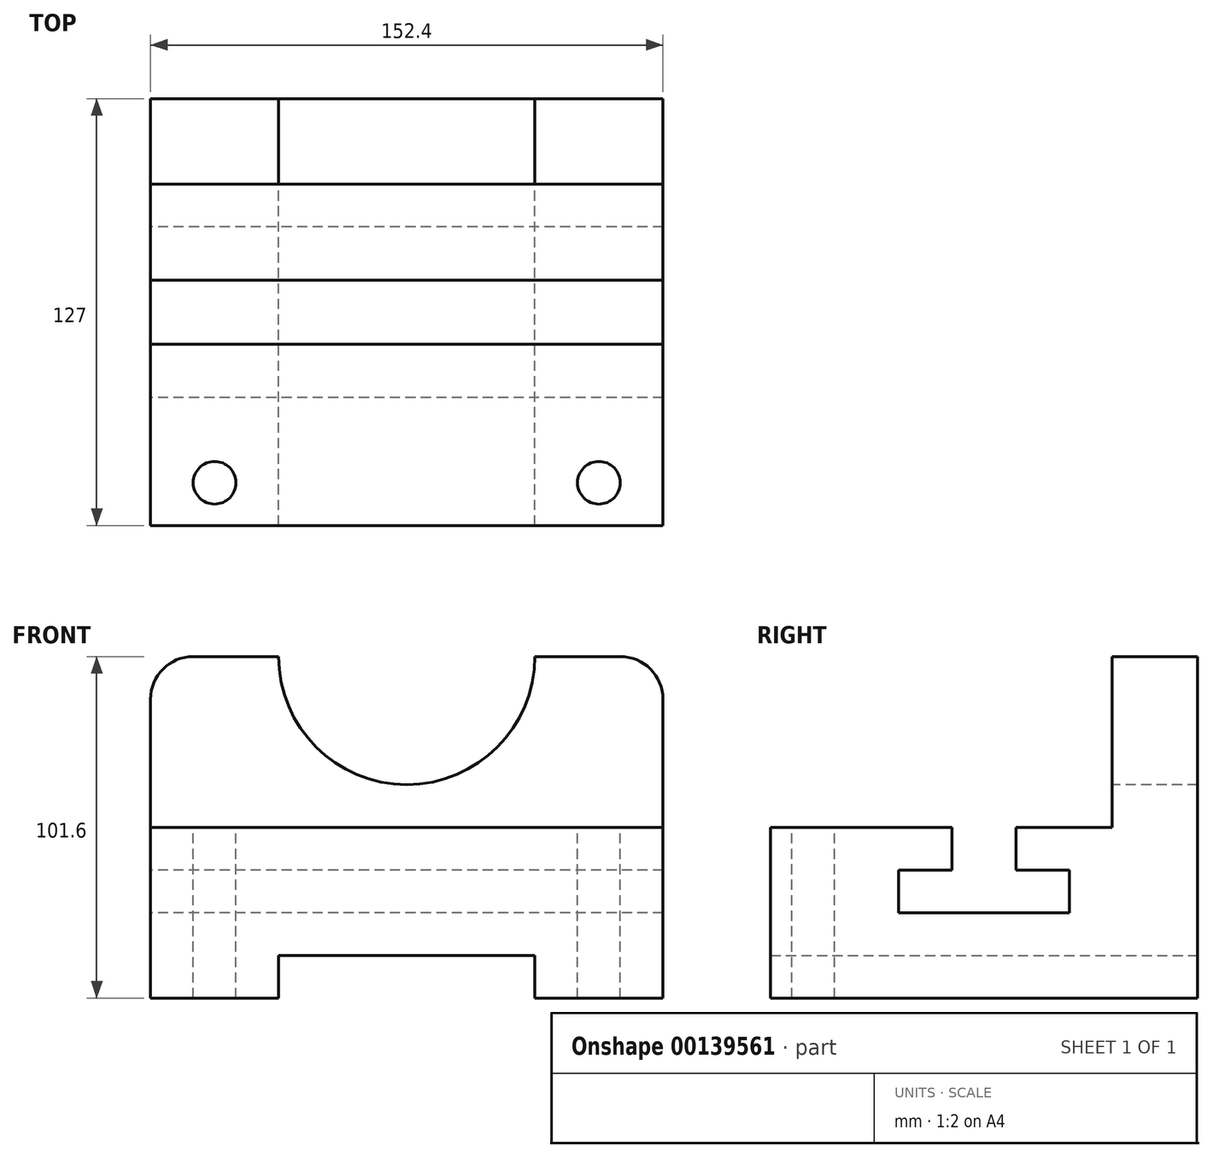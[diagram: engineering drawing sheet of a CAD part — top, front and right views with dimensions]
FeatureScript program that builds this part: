
annotation { "Feature Type Name" : "Feature", "Feature Type Description" : "" }
export const myFeature = defineFeature(function(context is Context, id is Id, definition is map)
    precondition{}
    {
        {
            var Q0;
            Q0=qCreatedBy(makeId("Right.planeOp"),FACE);
            var sketch = newSketch(context, id + "F0", { "sketchPlane" : qUnion([Q0])});
            skLineSegment(sketch, "E0", {"start": v(0, 0) * mm, "end": v(-127, 0) * mm});
            skLineSegment(sketch, "E1", {"start": v(0, 0) * mm, "end": v(0, 50.8) * mm});
            skLineSegment(sketch, "E2", {"start": v(0, 50.8) * mm, "end": v(-127, 50.8) * mm});
            skLineSegment(sketch, "E3", {"start": v(-127, 50.8) * mm, "end": v(-127, 0) * mm});
            skLineSegment(sketch, "E4", {"start": v(-53.98, 50.8) * mm, "end": v(-53.98, 38.1) * mm});
            skLineSegment(sketch, "E5", {"start": v(0, 50.8) * mm, "end": v(0, 101.6) * mm});
            skLineSegment(sketch, "E6", {"start": v(0, 101.6) * mm, "end": v(-25.4, 101.6) * mm});
            skLineSegment(sketch, "E7", {"start": v(-25.4, 101.6) * mm, "end": v(-25.4, 50.8) * mm});
            skLineSegment(sketch, "E8", {"start": v(-53.98, 38.1) * mm, "end": v(-38.1, 38.1) * mm});
            skLineSegment(sketch, "E9", {"start": v(-38.1, 38.1) * mm, "end": v(-38.1, 25.4) * mm});
            skLineSegment(sketch, "E10", {"start": v(-38.1, 25.4) * mm, "end": v(-88.9, 25.4) * mm});
            skLineSegment(sketch, "E11", {"start": v(-88.9, 25.4) * mm, "end": v(-88.9, 38.1) * mm});
            skLineSegment(sketch, "E12", {"start": v(-88.9, 38.1) * mm, "end": v(-73.03, 38.1) * mm});
            skLineSegment(sketch, "E13", {"start": v(-73.03, 38.1) * mm, "end": v(-73.03, 50.8) * mm});
            skSolve(sketch);
        }
        {
            var Q0;
            Q0=makeQuery(id+"F0.imprint","IMPRINT",FACE,{"disambiguationData":[TD([[makeQuery(id+"F0.imprint","IMPRINT",EDGE,{"derivedFrom":sQuery(id+"F0.wireOp",EDGE,"E0")}),-1.0]])]});
            extrude(context, id + "F1", {"entities" : qUnion([Q0]), "depth" : 152.4 * mm});
        }
        {
            var Q0;
            {var subQ0=sQuery(id+"F0.wireOp",EDGE,"E5");Q0=makeQuery(id+"F0.imprint","IMPRINT",FACE,{"disambiguationData":[TD([[makeQuery(id+"F0.imprint","IMPRINT",EDGE,{"derivedFrom":subQ0}),1.0]])]});}
            extrude(context, id + "F2", {"entities" : qUnion([Q0]), "operationType" : NewBodyOperationType.ADD, "depth" : 152.4 * mm});
        }
        {
            var Q0;
            Q0=makeQuery(id+"F2.opExtrude","CAP_EDGE",EDGE,{"disambiguationData":[OSD([sQuery(id+"F0.wireOp",EDGE,"E6")])],"isStart":true});
            fillet(context, id + "F3", {"entities" : qUnion([Q0]), "radius" : 12.7 * mm, "tangentPropagation" : true, "allowEdgeOverflow" : false});
        }
        {
            var Q0;
            Q0=makeQuery(id+"F2.opExtrude","CAP_EDGE",EDGE,{"disambiguationData":[OSD([sQuery(id+"F0.wireOp",EDGE,"E6")])],"isStart":false});
            fillet(context, id + "F4", {"entities" : qUnion([Q0]), "radius" : 12.7 * mm, "tangentPropagation" : true, "allowEdgeOverflow" : false});
        }
        {
            var Q0;
            Q0=qCreatedBy(makeId("Front.planeOp"),FACE);
            var sketch = newSketch(context, id + "F5", { "sketchPlane" : qUnion([Q0])});
            skLineSegment(sketch, "E14", {"start": v(38.1, 0) * mm, "end": v(38.1, 12.7) * mm});
            skLineSegment(sketch, "E15", {"start": v(38.1, 12.7) * mm, "end": v(114.3, 12.7) * mm});
            skLineSegment(sketch, "E16", {"start": v(114.3, 12.7) * mm, "end": v(114.3, 0) * mm});
            skLineSegment(sketch, "E17", {"start": v(38.1, 0) * mm, "end": v(114.3, 0) * mm});
            skSolve(sketch);
        }
        {
            var Q0;
            Q0 = qSketchRegion(id + "F5", true);
            extrude(context, id + "F6", {"entities" : qUnion([Q0]), "operationType" : NewBodyOperationType.REMOVE, "endBound" : BoundingType.THROUGH_ALL, "depth" : 25.4 * mm});
        }
        {
            var Q0;
            Q0=makeQuery(id+"F2.opExtrude","SWEPT_FACE",FACE,{"disambiguationData":[OSD([sQuery(id+"F0.wireOp",EDGE,"E7")])]});
            var sketch = newSketch(context, id + "F7", { "sketchPlane" : qUnion([Q0])});
            skCircle(sketch, "E18", {"center": v(76.2, 101.6) * mm, "radius": 38.1 * mm});
            skSolve(sketch);
        }
        {
            var Q0;
            {var subQ0=sQuery(id+"F7.wireOp",EDGE,"E18");var subQ1=makeQuery(id+"F2.opExtrude","SWEPT_EDGE",EDGE,{"disambiguationData":[OSD([sQuery(id+"F0.wireOp",EDGE,"E6"),sQuery(id+"F0.wireOp",EDGE,"E7")])]});var subQ2=makeQuery(id+"F7.imprint","INTERSECT",VERTEX,{"disambiguationData":[OD(0.0)],"derivedFrom":[subQ1,subQ0]});Q0=makeQuery(id+"F7.imprint","IMPRINT",FACE,{"disambiguationData":[TD([[makeQuery(id+"F7.imprint","IMPRINT",EDGE,{"disambiguationData":[TD([[subQ2,-1.0]])],"derivedFrom":subQ0}),1.0]])]});}
            extrude(context, id + "F8", {"entities" : qUnion([Q0]), "operationType" : NewBodyOperationType.REMOVE, "oppositeDirection" : true, "depth" : 152.4 * mm});
        }
        {
            var Q0;
            {var subQ0=sQuery(id+"F0.wireOp",EDGE,"E2");Q0=makeQuery(id+"F1.opExtrude","SWEPT_FACE",FACE,{"disambiguationData":[OSD([subQ0]),TDD([makeQuery(id+"F0.imprint","IMPRINT",EDGE,{"disambiguationData":[TD([[makeQuery(id+"F0.imprint","INTERSECT",VERTEX,{"derivedFrom":[subQ0,sQuery(id+"F0.wireOp",EDGE,"E3")]}),1.0]])],"derivedFrom":subQ0})])]});}
            var sketch = newSketch(context, id + "F9", { "sketchPlane" : qUnion([Q0])});
            skLineSegment(sketch, "E19.0", {"start": v(0, -73.03) * mm, "end": v(0, -127) * mm});
            skLineSegment(sketch, "E20.0", {"start": v(152.4, -73.03) * mm, "end": v(0, -73.03) * mm});
            skLineSegment(sketch, "E21.0", {"start": v(152.4, -127) * mm, "end": v(0, -127) * mm});
            skLineSegment(sketch, "E22.0", {"start": v(152.4, -73.03) * mm, "end": v(152.4, -127) * mm});
            skCircle(sketch, "E23", {"center": v(19.05, -114.3) * mm, "radius": 6.35 * mm});
            skCircle(sketch, "E24", {"center": v(133.35, -114.3) * mm, "radius": 6.35 * mm});
            skSolve(sketch);
        }
        {
            var Q0;
            Q0=makeQuery(id+"F9.imprint","IMPRINT",FACE,{"disambiguationData":[TD([[makeQuery(id+"F9.imprint","IMPRINT",EDGE,{"derivedFrom":sQuery(id+"F9.wireOp",EDGE,"E23")}),1.0]])]});
            var Q1;
            Q1=makeQuery(id+"F9.imprint","IMPRINT",FACE,{"disambiguationData":[TD([[makeQuery(id+"F9.imprint","IMPRINT",EDGE,{"derivedFrom":sQuery(id+"F9.wireOp",EDGE,"E24")}),1.0]])]});
            extrude(context, id + "F10", {"entities" : qUnion([Q0, Q1]), "operationType" : NewBodyOperationType.REMOVE, "oppositeDirection" : true, "depth" : 152.4 * mm});
        }
    });
